FREECAD ASSEMBLY — COMPONENT RECIPES ("AB25_assembly")

This assembly document has 3 components, labeled P0..P2 below (a component is one placed body or linked part). 0 of them carry a construction recipe — the FreeCAD feature program that regenerates the part from scratch, quoted from this document or its linked companion documents; the rest are supplied as boundary geometry only. No exploded tour is included for this assembly.
COMPONENT P0 — geometry summary ("Body"; no construction recipe available for this part):
  bounding box: 60.0 x 40.0 x 30.0 mm
  tessellated surface: 10,900 triangles
  volume: 33532 mm^3 (47% of its bounding box)
  symmetry: 2-fold rotationally symmetric about the z axis; mirror-symmetric across its x mid-plane, y mid-plane
COMPONENT P1 — geometry summary ("Body001"; no construction recipe available for this part):
  bounding box: 126.0 x 67.0 x 20.0 mm
  tessellated surface: 11,964 triangles
  volume: 57875 mm^3 (34% of its bounding box)
  symmetry: mirror-symmetric across its x mid-plane
COMPONENT P2 — geometry summary ("Body002"; no construction recipe available for this part):
  bounding box: 30.0 x 28.0 x 17.5 mm
  tessellated surface: 7,312 triangles
  volume: 11747 mm^3 (80% of its bounding box)
  symmetry: mirror-symmetric across its z mid-plane
PROVENANCE & LICENSES
A FreeCAD (.FCStd) document from a public repository crawl; recipes are the document's own serialized feature recipes (and, for linked parts, companion documents' recipes).
License: as declared in the source repository (recorded in the dataset sidecar).
